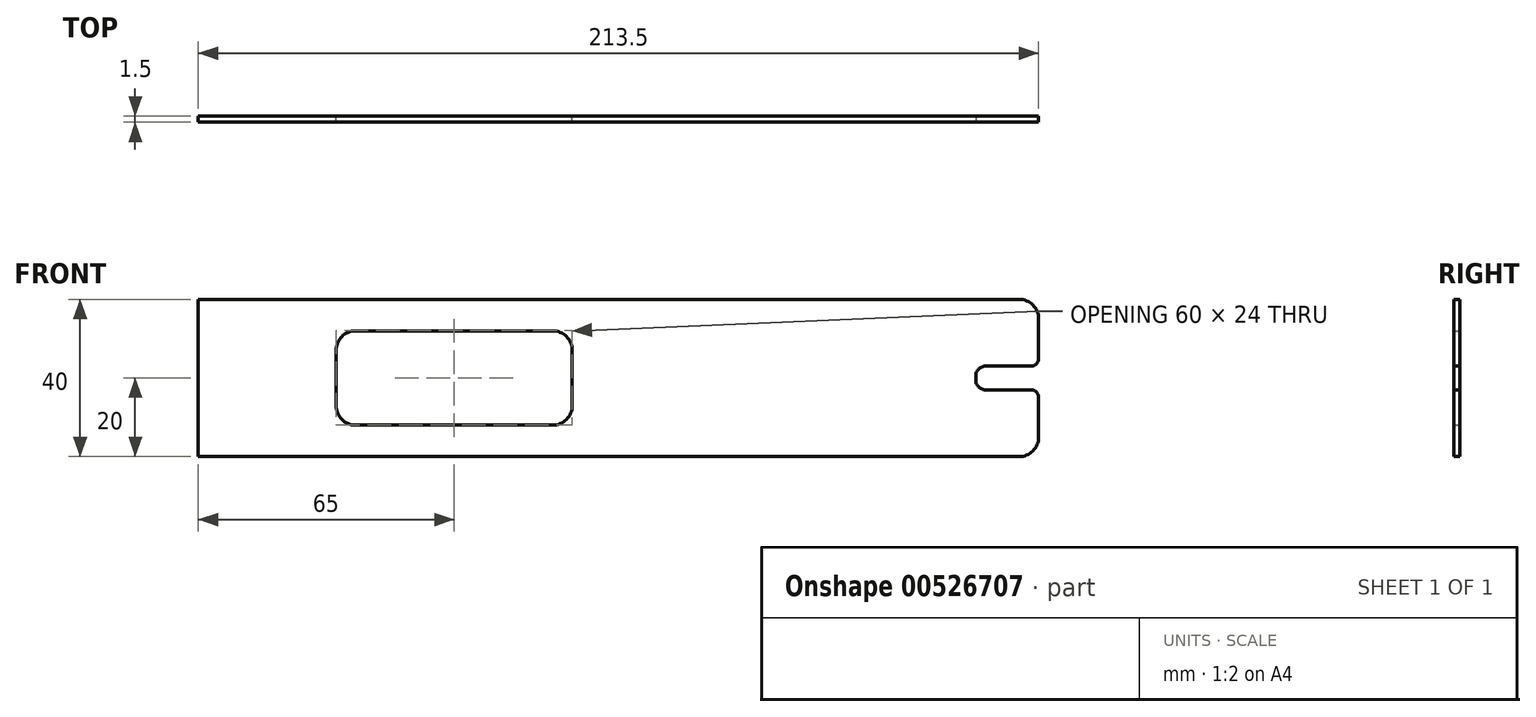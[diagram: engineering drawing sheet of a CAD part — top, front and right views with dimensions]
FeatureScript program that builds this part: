
annotation { "Feature Type Name" : "Feature", "Feature Type Description" : "" }
export const myFeature = defineFeature(function(context is Context, id is Id, definition is map)
    precondition{}
    {
        {
            var Q0;
            Q0=qCreatedBy(makeId("Front.planeOp"),FACE);
            var sketch = newSketch(context, id + "F0", { "sketchPlane" : qUnion([Q0])});
            skLineSegment(sketch, "E0.bottom", {"start": v(-65, -40) * mm, "end": v(0, -40) * mm});
            skLineSegment(sketch, "E0.top", {"start": v(-65, 0) * mm, "end": v(0, 0) * mm});
            skLineSegment(sketch, "E0.left", {"start": v(-65, -40) * mm, "end": v(-65, 0) * mm});
            skPoint(sketch, "E0.middle", {"position": v(0, 0) * mm});
            skLineSegment(sketch, "E1.bottom", {"start": v(-25, -32) * mm, "end": v(10.58, -32) * mm});
            skLineSegment(sketch, "E1.top", {"start": v(-25, -8) * mm, "end": v(0, -8) * mm});
            skLineSegment(sketch, "E1.left", {"start": v(-30, -27) * mm, "end": v(-30, -13) * mm});
            skPoint(sketch, "E2.visualSharp", {"position": v(-30, -32) * mm});
            skArc(sketch, "E2.filletArc", {"start": v(-30, -27) * mm, "mid": v(-28.54, -30.54) * mm, "end": v(-25, -32) * mm});
            skPoint(sketch, "E3.visualSharp", {"position": v(-30, -8) * mm});
            skArc(sketch, "E3.filletArc", {"start": v(-25, -8) * mm, "mid": v(-28.54, -9.46) * mm, "end": v(-30, -13) * mm});
            skLineSegment(sketch, "E4", {"start": v(-65, -20) * mm, "end": v(-30, -20) * mm, "construction": true});
            skLineSegment(sketch, "E5", {"start": v(-30, -20) * mm, "end": v(0, -20) * mm, "construction": true});
            skLineSegment(sketch, "E6.MirrorCS", {"start": v(30, -27) * mm, "end": v(30, -13) * mm});
            skArc(sketch, "E7.MirrorCS", {"start": v(25, -8) * mm, "mid": v(28.54, -9.46) * mm, "end": v(30, -13) * mm});
            skLineSegment(sketch, "E8.MirrorCS", {"start": v(65, -40) * mm, "end": v(0, -40) * mm});
            skLineSegment(sketch, "E9.MirrorCS", {"start": v(65, 0) * mm, "end": v(0, 0) * mm});
            skArc(sketch, "E10.MirrorCS", {"start": v(30, -27) * mm, "mid": v(28.54, -30.54) * mm, "end": v(25, -32) * mm});
            skLineSegment(sketch, "E11.MirrorCS", {"start": v(30, -20) * mm, "end": v(0, -20) * mm, "construction": true});
            skPoint(sketch, "E12.MirrorP", {"position": v(30, -8) * mm});
            skPoint(sketch, "E13.MirrorP", {"position": v(30, -32) * mm});
            skLineSegment(sketch, "E14.MirrorCS", {"start": v(65, -40) * mm, "end": v(65, 0) * mm});
            skLineSegment(sketch, "E15.MirrorCS", {"start": v(25, -32) * mm, "end": v(-10.58, -32) * mm});
            skLineSegment(sketch, "E16.MirrorCS", {"start": v(25, -8) * mm, "end": v(0, -8) * mm});
            skLineSegment(sketch, "E17.MirrorCS", {"start": v(65, -20) * mm, "end": v(30, -20) * mm, "construction": true});
            skSolve(sketch);
        }
        {
            var Q0;
            {var subQ1=sQuery(id+"F0.wireOp",EDGE,"BZA0fC5U-b41i-V4vY-fGkc-xttjDSqdq4Qw.left");Q0=makeQuery(id+"F0.imprint","IMPRINT",FACE,{"disambiguationData":[TD([[makeQuery(id+"F0.imprint","IMPRINT",EDGE,{"derivedFrom":subQ1}),1.0]])]});}
            var Q1;
            {var subQ0=sQuery(id+"F0.wireOp",EDGE,"E0.left");Q1=makeQuery(id+"F0.imprint","IMPRINT",FACE,{"disambiguationData":[TD([[makeQuery(id+"F0.imprint","IMPRINT",EDGE,{"derivedFrom":subQ0}),1.0]])]});}
            var Q2;
            {var subQ1=sQuery(id+"F0.wireOp",EDGE,"E0.left");Q2=makeQuery(id+"F0.imprint","IMPRINT",FACE,{"disambiguationData":[TD([[makeQuery(id+"F0.imprint","IMPRINT",EDGE,{"derivedFrom":subQ1}),-1.0]])]});}
            var Q3;
            {var subQ0=sQuery(id+"F0.wireOp",EDGE,"E14.MirrorCS");Q3=makeQuery(id+"F0.imprint","IMPRINT",FACE,{"disambiguationData":[TD([[makeQuery(id+"F0.imprint","IMPRINT",EDGE,{"derivedFrom":subQ0}),-1.0]])]});}
            var Q4;
            {var subQ2=sQuery(id+"F0.wireOp",EDGE,"82465405-fadb-4a58-8aac-de200895b3954.MirrorCS");Q4=makeQuery(id+"F0.imprint","IMPRINT",FACE,{"disambiguationData":[TD([[makeQuery(id+"F0.imprint","IMPRINT",EDGE,{"derivedFrom":subQ2}),-1.0]])]});}
            extrude(context, id + "F1", {"entities" : qUnion([Q0, Q1, Q2, Q3, Q4]), "depth" : 1.5 * mm});
        }
        {
            var Q0;
            Q0=makeQuery(id+"F1.opExtrude","CAP_FACE",FACE,{"disambiguationData":[OSD([sQuery(id+"F0.wireOp",EDGE,"E0.left"),sQuery(id+"F0.wireOp",EDGE,"E1.bottom"),sQuery(id+"F0.wireOp",EDGE,"E1.top"),sQuery(id+"F0.wireOp",EDGE,"E1.left"),sQuery(id+"F0.wireOp",EDGE,"E2.filletArc"),sQuery(id+"F0.wireOp",EDGE,"E3.filletArc"),sQuery(id+"F0.wireOp",EDGE,"E6.MirrorCS"),sQuery(id+"F0.wireOp",EDGE,"E7.MirrorCS"),sQuery(id+"F0.wireOp",EDGE,"E10.MirrorCS"),sQuery(id+"F0.wireOp",EDGE,"E14.MirrorCS"),sQuery(id+"F0.wireOp",EDGE,"E15.MirrorCS"),sQuery(id+"F0.wireOp",EDGE,"E16.MirrorCS"),sQuery(id+"F0.wireOp",EDGE,"E9.MirrorCS"),sQuery(id+"F0.wireOp",EDGE,"E8.MirrorCS"),sQuery(id+"F0.wireOp",EDGE,"E0.top"),sQuery(id+"F0.wireOp",EDGE,"E0.bottom")])],"isStart":false});
            var sketch = newSketch(context, id + "F2", { "sketchPlane" : qUnion([Q0])});
            skLineSegment(sketch, "E18.bottom", {"start": v(65, 0) * mm, "end": v(67, 0) * mm});
            skLineSegment(sketch, "E18.top", {"start": v(65, -40) * mm, "end": v(67, -40) * mm});
            skLineSegment(sketch, "E18.left", {"start": v(65, 0) * mm, "end": v(65, -40) * mm});
            skLineSegment(sketch, "E18.right", {"start": v(67, 0) * mm, "end": v(67, -40) * mm});
            skSolve(sketch);
        }
        {
            var Q0;
            Q0=qSketchRegion(id+"F2",true);
            extrude(context, id + "F3", {"entities" : qUnion([Q0]), "operationType" : NewBodyOperationType.ADD, "oppositeDirection" : true, "depth" : 1.5 * mm});
        }
        {
            var Q0;
            Q0=makeQuery(id+"F3.boolean.opBoolean","MERGE",FACE,{"derivedFrom":[makeQuery(id+"F1.opExtrude","CAP_FACE",FACE,{"disambiguationData":[OSD([sQuery(id+"F0.wireOp",EDGE,"E0.left"),sQuery(id+"F0.wireOp",EDGE,"E1.bottom"),sQuery(id+"F0.wireOp",EDGE,"E1.top"),sQuery(id+"F0.wireOp",EDGE,"E1.left"),sQuery(id+"F0.wireOp",EDGE,"E2.filletArc"),sQuery(id+"F0.wireOp",EDGE,"E3.filletArc"),sQuery(id+"F0.wireOp",EDGE,"E6.MirrorCS"),sQuery(id+"F0.wireOp",EDGE,"E7.MirrorCS"),sQuery(id+"F0.wireOp",EDGE,"E10.MirrorCS"),sQuery(id+"F0.wireOp",EDGE,"E14.MirrorCS"),sQuery(id+"F0.wireOp",EDGE,"E15.MirrorCS"),sQuery(id+"F0.wireOp",EDGE,"E16.MirrorCS"),sQuery(id+"F0.wireOp",EDGE,"E9.MirrorCS"),sQuery(id+"F0.wireOp",EDGE,"E8.MirrorCS"),sQuery(id+"F0.wireOp",EDGE,"E0.top"),sQuery(id+"F0.wireOp",EDGE,"E0.bottom")])],"isStart":false}),makeQuery(id+"F3.opExtrude","CAP_FACE",FACE,{"disambiguationData":[OSD([sQuery(id+"F2.wireOp",EDGE,"E18.bottom"),sQuery(id+"F2.wireOp",EDGE,"E18.top"),sQuery(id+"F2.wireOp",EDGE,"E18.left"),sQuery(id+"F2.wireOp",EDGE,"E18.right")])],"isStart":true})]});
            var sketch = newSketch(context, id + "F4", { "sketchPlane" : qUnion([Q0])});
            skLineSegment(sketch, "E19.bottom", {"start": v(67, 0) * mm, "end": v(143.5, 0) * mm});
            skLineSegment(sketch, "E19.top", {"start": v(67, -40) * mm, "end": v(143.5, -40) * mm});
            skLineSegment(sketch, "E19.left", {"start": v(67, 0) * mm, "end": v(67, -40) * mm});
            skLineSegment(sketch, "E19.right", {"start": v(148.5, -5) * mm, "end": v(148.5, -15) * mm});
            skPoint(sketch, "E20.visualSharp", {"position": v(148.5, 0) * mm});
            skArc(sketch, "E20.filletArc", {"start": v(148.5, -5) * mm, "mid": v(147.04, -1.46) * mm, "end": v(143.5, 0) * mm});
            skPoint(sketch, "E21.visualSharp", {"position": v(148.5, -40) * mm});
            skArc(sketch, "E21.filletArc", {"start": v(143.5, -40) * mm, "mid": v(147.04, -38.54) * mm, "end": v(148.5, -35) * mm});
            skLineSegment(sketch, "E22", {"start": v(148.5, -20) * mm, "end": v(144.5, -20) * mm});
            skLineSegment(sketch, "E23", {"start": v(144.5, -20) * mm, "end": v(138.5, -20) * mm});
            skLineSegment(sketch, "E24.bottom", {"start": v(142, -23) * mm, "end": v(135, -23) * mm});
            skLineSegment(sketch, "E24.top", {"start": v(142, -17) * mm, "end": v(135, -17) * mm});
            skLineSegment(sketch, "E24.left", {"start": v(144.5, -20.5) * mm, "end": v(144.5, -19.5) * mm});
            skLineSegment(sketch, "E24.right", {"start": v(132.5, -20.5) * mm, "end": v(132.5, -19.5) * mm});
            skPoint(sketch, "E24.middle", {"position": v(138.5, -20) * mm});
            skPoint(sketch, "E25.visualSharp", {"position": v(132.5, -17) * mm});
            skArc(sketch, "E25.filletArc", {"start": v(135, -17) * mm, "mid": v(133.23, -17.73) * mm, "end": v(132.5, -19.5) * mm});
            skPoint(sketch, "E26.visualSharp", {"position": v(132.5, -23) * mm});
            skArc(sketch, "E26.filletArc", {"start": v(132.5, -20.5) * mm, "mid": v(133.23, -22.27) * mm, "end": v(135, -23) * mm});
            skPoint(sketch, "E27.visualSharp", {"position": v(144.5, -17) * mm});
            skArc(sketch, "E27.filletArc", {"start": v(144.5, -19.5) * mm, "mid": v(143.77, -17.73) * mm, "end": v(142, -17) * mm});
            skPoint(sketch, "E28.visualSharp", {"position": v(144.5, -23) * mm});
            skArc(sketch, "E28.filletArc", {"start": v(142, -23) * mm, "mid": v(143.77, -22.27) * mm, "end": v(144.5, -20.5) * mm});
            skLineSegment(sketch, "E29", {"start": v(142, -17) * mm, "end": v(146.5, -17) * mm});
            skLineSegment(sketch, "E30", {"start": v(148.5, -12) * mm, "end": v(148.5, -17.12) * mm});
            skLineSegment(sketch, "E31", {"start": v(142, -23) * mm, "end": v(146.5, -23) * mm});
            skPoint(sketch, "E32.newPointB", {"position": v(148.5, -35) * mm});
            skArc(sketch, "E32.filletArc", {"start": v(146.5, -17) * mm, "mid": v(147.91, -16.41) * mm, "end": v(148.5, -15) * mm});
            skLineSegment(sketch, "E33", {"start": v(148.5, -35) * mm, "end": v(148.5, -25) * mm});
            skPoint(sketch, "E34.visualSharp", {"position": v(148.5, -23) * mm});
            skArc(sketch, "E34.filletArc", {"start": v(148.5, -25) * mm, "mid": v(147.91, -23.59) * mm, "end": v(146.5, -23) * mm});
            skSolve(sketch);
        }
        {
            var Q0;
            Q0=makeQuery(id+"F4.imprint","IMPRINT",FACE,{"disambiguationData":[TD([[makeQuery(id+"F4.imprint","IMPRINT",EDGE,{"derivedFrom":sQuery(id+"F4.wireOp",EDGE,"E19.bottom")}),-1.0]])]});
            extrude(context, id + "F5", {"entities" : qUnion([Q0]), "operationType" : NewBodyOperationType.ADD, "oppositeDirection" : true, "depth" : 1.5 * mm});
        }
    });
